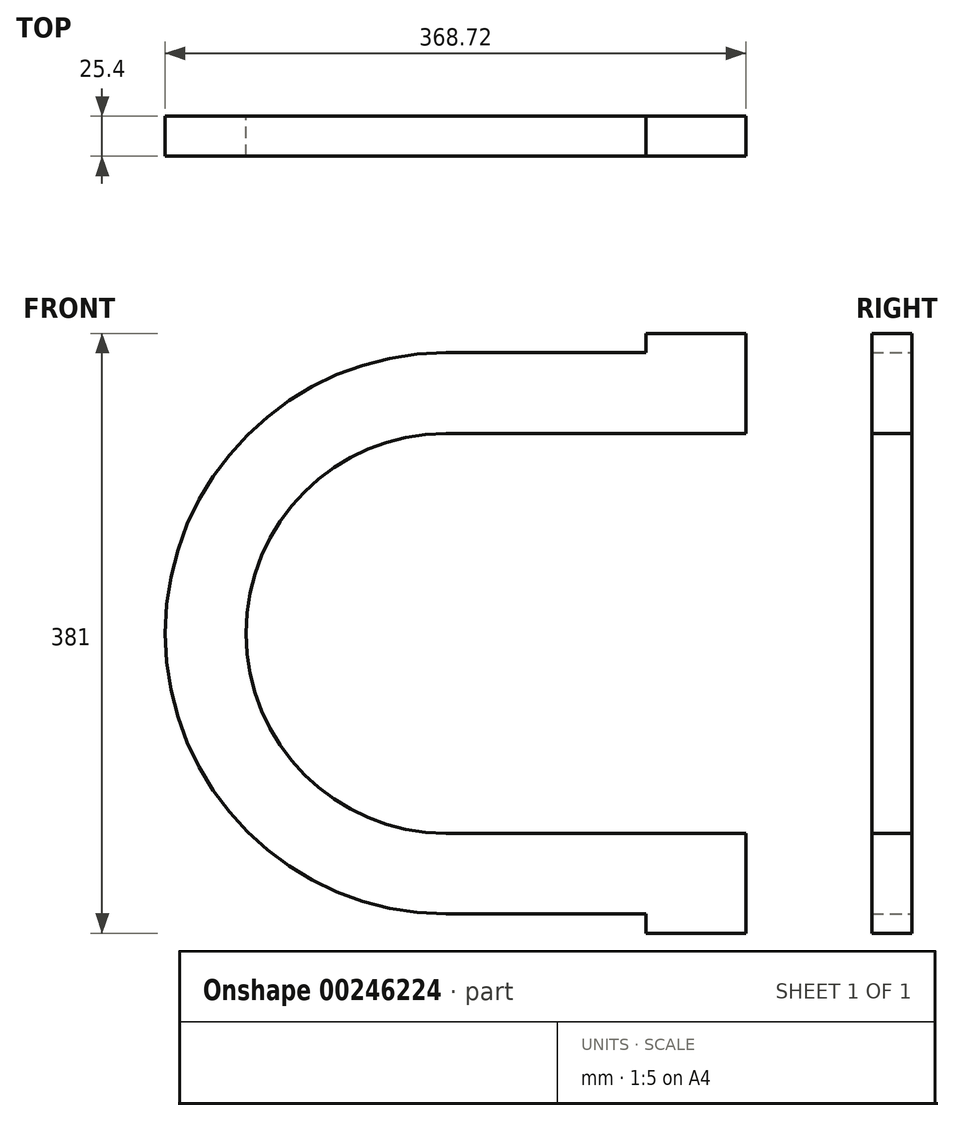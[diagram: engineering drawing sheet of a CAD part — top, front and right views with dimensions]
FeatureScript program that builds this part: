
annotation { "Feature Type Name" : "Feature", "Feature Type Description" : "" }
export const myFeature = defineFeature(function(context is Context, id is Id, definition is map)
    precondition{}
    {
        {
            var Q0;
            Q0=qCreatedBy(makeId("Front.planeOp"),FACE);
            var sketch = newSketch(context, id + "F0", { "sketchPlane" : qUnion([Q0])});
            skLineSegment(sketch, "E0.bottom", {"start": v(127, 178.22) * mm, "end": v(0, 178.22) * mm});
            skLineSegment(sketch, "E0.top", {"start": v(127, -178.22) * mm, "end": v(0, -178.22) * mm});
            skLineSegment(sketch, "E0.left", {"start": v(190.5, 178.22) * mm, "end": v(190.5, 127) * mm});
            skPoint(sketch, "E0.middle", {"position": v(0, 0) * mm});
            skArc(sketch, "E1", {"start": v(0, 127) * mm, "mid": v(-127, 0) * mm, "end": v(0, -127) * mm});
            skLineSegment(sketch, "E2", {"start": v(0, -127) * mm, "end": v(190.5, -127) * mm});
            skLineSegment(sketch, "E3", {"start": v(0, 127) * mm, "end": v(190.5, 127) * mm});
            skLineSegment(sketch, "E4.bottom", {"start": v(190.5, -127) * mm, "end": v(127, -127) * mm});
            skLineSegment(sketch, "E4.top", {"start": v(190.5, -190.5) * mm, "end": v(127, -190.5) * mm});
            skLineSegment(sketch, "E4.left", {"start": v(190.5, -127) * mm, "end": v(190.5, -190.5) * mm});
            skLineSegment(sketch, "E4.right", {"start": v(127, -178.22) * mm, "end": v(127, -190.5) * mm});
            skLineSegment(sketch, "E5.bottom", {"start": v(190.5, 127) * mm, "end": v(127, 127) * mm});
            skLineSegment(sketch, "E5.top", {"start": v(190.5, 190.5) * mm, "end": v(127, 190.5) * mm});
            skLineSegment(sketch, "E5.left", {"start": v(190.5, 127) * mm, "end": v(190.5, 190.5) * mm});
            skLineSegment(sketch, "E5.right", {"start": v(127, 178.22) * mm, "end": v(127, 190.5) * mm});
            skLineSegment(sketch, "E6.trimOffspring", {"start": v(190.5, -127) * mm, "end": v(190.5, -178.22) * mm});
            skArc(sketch, "E7", {"start": v(0, 178.22) * mm, "mid": v(-178.22, 0) * mm, "end": v(0, -178.22) * mm});
            skSolve(sketch);
        }
        {
            var Q0;
            Q0=makeQuery(id+"F0.imprint","IMPRINT",FACE,{"disambiguationData":[TD([[makeQuery(id+"F0.imprint","IMPRINT",EDGE,{"derivedFrom":sQuery(id+"F0.wireOp",EDGE,"E0.bottom")}),1.0]])]});
            extrude(context, id + "F1", {"entities" : qUnion([Q0]), "depth" : 25.4 * mm});
        }
    });
